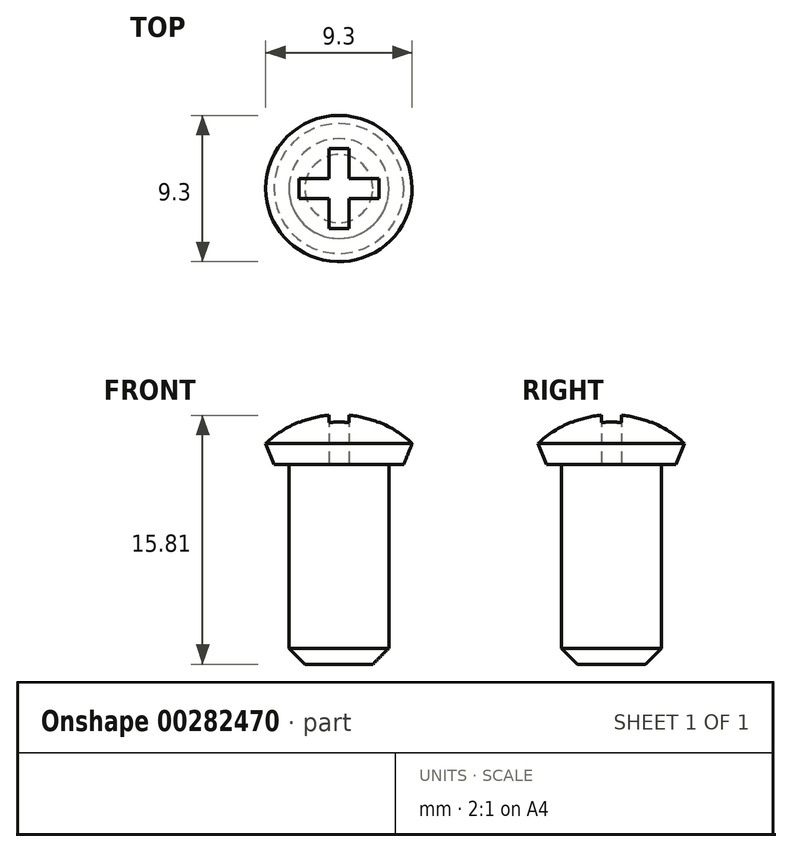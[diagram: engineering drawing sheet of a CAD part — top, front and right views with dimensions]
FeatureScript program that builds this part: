
annotation { "Feature Type Name" : "Feature", "Feature Type Description" : "" }
export const myFeature = defineFeature(function(context is Context, id is Id, definition is map)
    precondition{}
    {
        {
            var Q0;
            Q0=qCreatedBy(makeId("Front.planeOp"),FACE);
            var sketch = newSketch(context, id + "F0", { "sketchPlane" : qUnion([Q0])});
            skLineSegment(sketch, "E0", {"start": v(5.71, 0) * mm, "end": v(3.17, 0) * mm});
            skLineSegment(sketch, "E1", {"start": v(3.17, 0) * mm, "end": v(3.18, -12.7) * mm});
            skLineSegment(sketch, "E2", {"start": v(3.18, -12.7) * mm, "end": v(0, -12.7) * mm});
            skLineSegment(sketch, "E3", {"start": v(0, -12.7) * mm, "end": v(0, 3.18) * mm});
            skArc(sketch, "E4", {"start": v(5.72, 0) * mm, "mid": v(3.27, 2.33) * mm, "end": v(0, 3.18) * mm});
            skLineSegment(sketch, "E5", {"start": v(0, -12.7) * mm, "end": v(0, -23.97) * mm, "construction": true});
            skSolve(sketch);
        }
        {
            var Q0;
            Q0=makeQuery(id+"F0.imprint","IMPRINT",FACE,{"disambiguationData":[TD([[makeQuery(id+"F0.imprint","IMPRINT",EDGE,{"derivedFrom":sQuery(id+"F0.wireOp",EDGE,"E0")}),-1.0]])]});
            var Q1;
            Q1=sQuery(id+"F0.wireOp",EDGE,"E3");
            revolve(context, id + "F1", {"entities" : qUnion([Q0]), "axis" : qUnion([Q1]), "revolveType" : RevolveType.FULL});
        }
        {
            var Q0;
            Q0=makeQuery(id+"F1.opRevolve","SWEPT_EDGE",EDGE,{"disambiguationData":[OSD([sQuery(id+"F0.wireOp",EDGE,"E0"),sQuery(id+"F0.wireOp",EDGE,"E4")])]});
            chamfer(context, id + "F2", {"entities" : qUnion([Q0]), "width" : 0.76 * mm, "tangentPropagation" : true});
        }
        {
            var Q0;
            Q0=qCreatedBy(makeId("Top.planeOp"),FACE);
            var sketch = newSketch(context, id + "F3", { "sketchPlane" : qUnion([Q0])});
            skLineSegment(sketch, "E6", {"start": v(-6.83, 0) * mm, "end": v(6.52, 0) * mm, "construction": true});
            skLineSegment(sketch, "E7", {"start": v(0, 5.39) * mm, "end": v(0, -6.35) * mm, "construction": true});
            skLineSegment(sketch, "E8.bottom", {"start": v(-0.64, 2.54) * mm, "end": v(0.63, 2.54) * mm});
            skLineSegment(sketch, "E8.top", {"start": v(-0.63, -2.54) * mm, "end": v(0.63, -2.54) * mm});
            skLineSegment(sketch, "E8.left", {"start": v(-0.64, 2.54) * mm, "end": v(-0.64, 0.63) * mm});
            skLineSegment(sketch, "E8.right", {"start": v(0.64, 2.54) * mm, "end": v(0.64, 0.63) * mm});
            skLineSegment(sketch, "E9.bottom", {"start": v(-2.54, 0.64) * mm, "end": v(-0.64, 0.64) * mm});
            skLineSegment(sketch, "E9.top", {"start": v(-2.54, -0.63) * mm, "end": v(-0.64, -0.63) * mm});
            skLineSegment(sketch, "E9.left", {"start": v(-2.54, 0.63) * mm, "end": v(-2.54, -0.63) * mm});
            skLineSegment(sketch, "E9.right", {"start": v(2.54, 0.64) * mm, "end": v(2.54, -0.63) * mm});
            skLineSegment(sketch, "E10.trimOffspring", {"start": v(0.63, 0.64) * mm, "end": v(2.54, 0.64) * mm});
            skLineSegment(sketch, "E11.trimOffspring", {"start": v(0.64, -0.63) * mm, "end": v(0.64, -2.54) * mm});
            skLineSegment(sketch, "E12.trimOffspring", {"start": v(-0.64, -0.63) * mm, "end": v(-0.64, -2.54) * mm});
            skLineSegment(sketch, "E13.trimOffspring", {"start": v(0.64, -0.63) * mm, "end": v(2.54, -0.63) * mm});
            skSolve(sketch);
        }
        {
            var Q0;
            Q0=qSketchRegion(id+"F3",true);
            extrude(context, id + "F4", {"entities" : qUnion([Q0]), "operationType" : NewBodyOperationType.REMOVE, "endBound" : BoundingType.THROUGH_ALL, "depth" : 25.4 * mm});
        }
        {
            var Q0;
            Q0=makeQuery(id+"F1.opRevolve","SWEPT_EDGE",EDGE,{"disambiguationData":[OSD([sQuery(id+"F0.wireOp",EDGE,"E1"),sQuery(id+"F0.wireOp",EDGE,"E2")])]});
            chamfer(context, id + "F5", {"entities" : qUnion([Q0]), "width" : 1.02 * mm, "tangentPropagation" : true});
        }
    });
